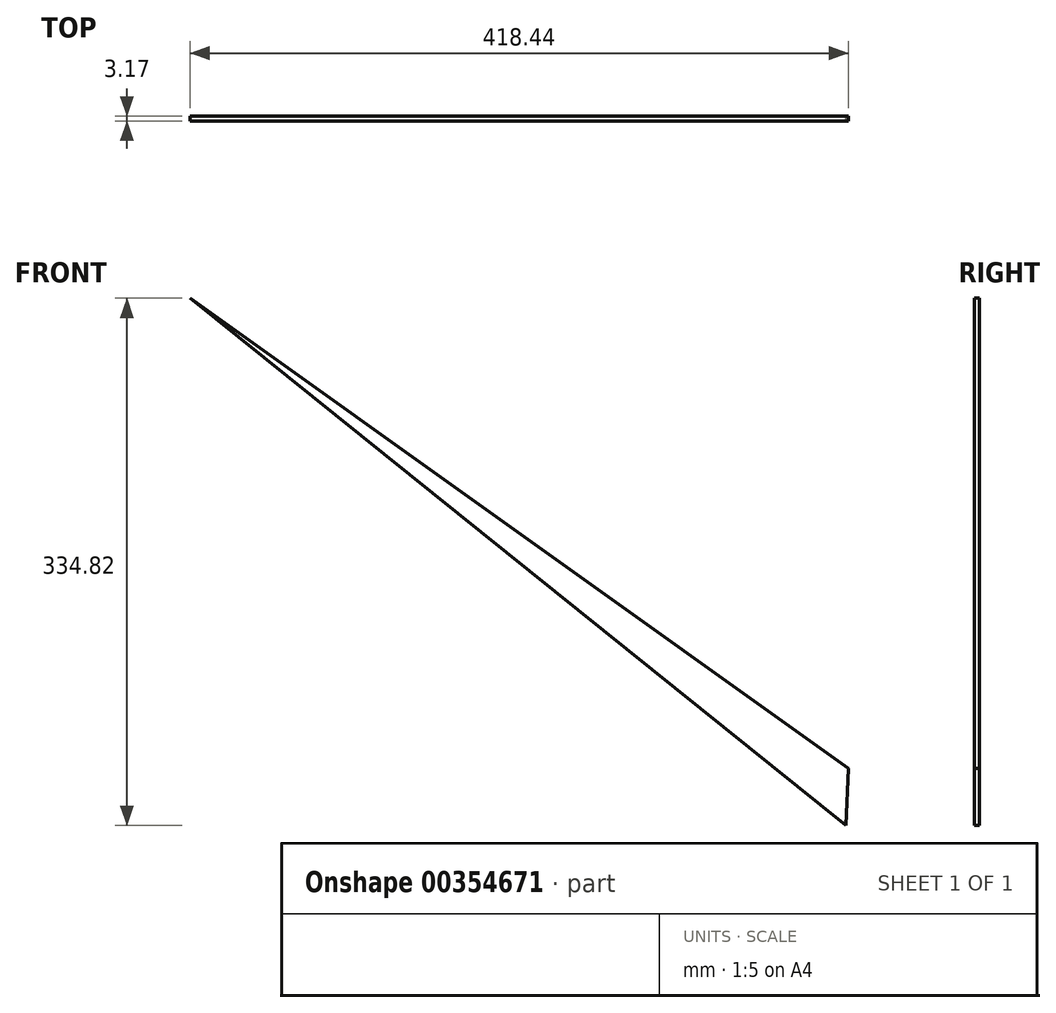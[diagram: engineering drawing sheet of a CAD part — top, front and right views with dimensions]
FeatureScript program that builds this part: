
annotation { "Feature Type Name" : "Feature", "Feature Type Description" : "" }
export const myFeature = defineFeature(function(context is Context, id is Id, definition is map)
    precondition{}
    {
        {
            var Q0;
            Q0=qCreatedBy(makeId("Front.planeOp"),FACE);
            var sketch = newSketch(context, id + "F0", { "sketchPlane" : qUnion([Q0])});
            skLineSegment(sketch, "E0", {"start": v(0, 0) * mm, "end": v(-418.44, 298.67) * mm});
            skLineSegment(sketch, "E1", {"start": v(-418.44, 298.67) * mm, "end": v(-1.59, -36.15) * mm});
            skLineSegment(sketch, "E2", {"start": v(-1.59, -36.15) * mm, "end": v(0, 0) * mm});
            skSolve(sketch);
        }
        {
            var Q0;
            Q0=qSketchRegion(id+"F0",true);
            extrude(context, id + "F1", {"entities" : qUnion([Q0]), "depth" : 3.17 * mm});
        }
    });
